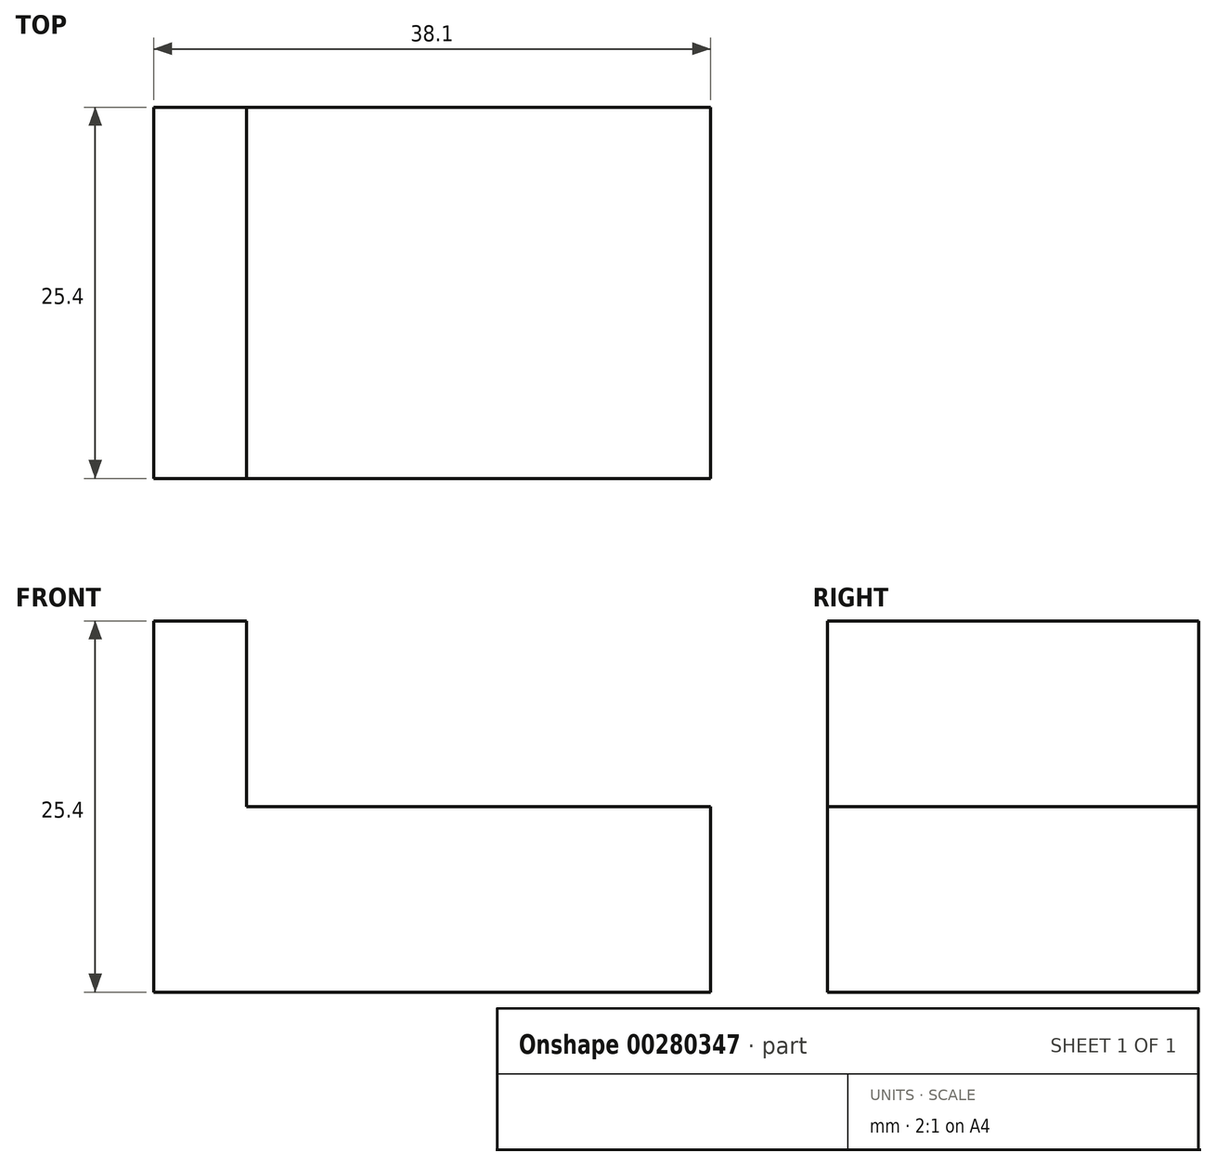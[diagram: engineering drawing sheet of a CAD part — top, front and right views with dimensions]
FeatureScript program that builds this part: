
annotation { "Feature Type Name" : "Feature", "Feature Type Description" : "" }
export const myFeature = defineFeature(function(context is Context, id is Id, definition is map)
    precondition{}
    {
        {
            var Q0;
            Q0=qCreatedBy(makeId("Top.planeOp"),FACE);
            var sketch = newSketch(context, id + "F0", { "sketchPlane" : qUnion([Q0])});
            skLineSegment(sketch, "E0.bottom", {"start": v(0, 0) * mm, "end": v(38.1, 0) * mm});
            skLineSegment(sketch, "E0.top", {"start": v(0, 25.4) * mm, "end": v(38.1, 25.4) * mm});
            skLineSegment(sketch, "E0.left", {"start": v(0, 0) * mm, "end": v(0, 25.4) * mm});
            skLineSegment(sketch, "E0.right", {"start": v(38.1, 0) * mm, "end": v(38.1, 25.4) * mm});
            skLineSegment(sketch, "E1", {"start": v(0, 0) * mm, "end": v(6.35, 0) * mm});
            skLineSegment(sketch, "E2", {"start": v(6.35, 0) * mm, "end": v(6.35, 25.4) * mm});
            skSolve(sketch);
        }
        {
            var Q0;
            {var subQ0=sQuery(id+"F0.wireOp",EDGE,"E0.left");Q0=makeQuery(id+"F0.imprint","IMPRINT",FACE,{"disambiguationData":[TD([[makeQuery(id+"F0.imprint","IMPRINT",EDGE,{"derivedFrom":subQ0}),-1.0]])]});}
            extrude(context, id + "F1", {"entities" : qUnion([Q0]), "depth" : 25.4 * mm});
        }
        {
            var Q0;
            Q0=makeQuery(id+"F0.imprint","IMPRINT",FACE,{"disambiguationData":[TD([[makeQuery(id+"F0.imprint","IMPRINT",EDGE,{"derivedFrom":sQuery(id+"F0.wireOp",EDGE,"E0.bottom")}),1.0]])]});
            extrude(context, id + "F2", {"entities" : qUnion([Q0]), "operationType" : NewBodyOperationType.ADD, "depth" : 12.7 * mm});
        }
    });
